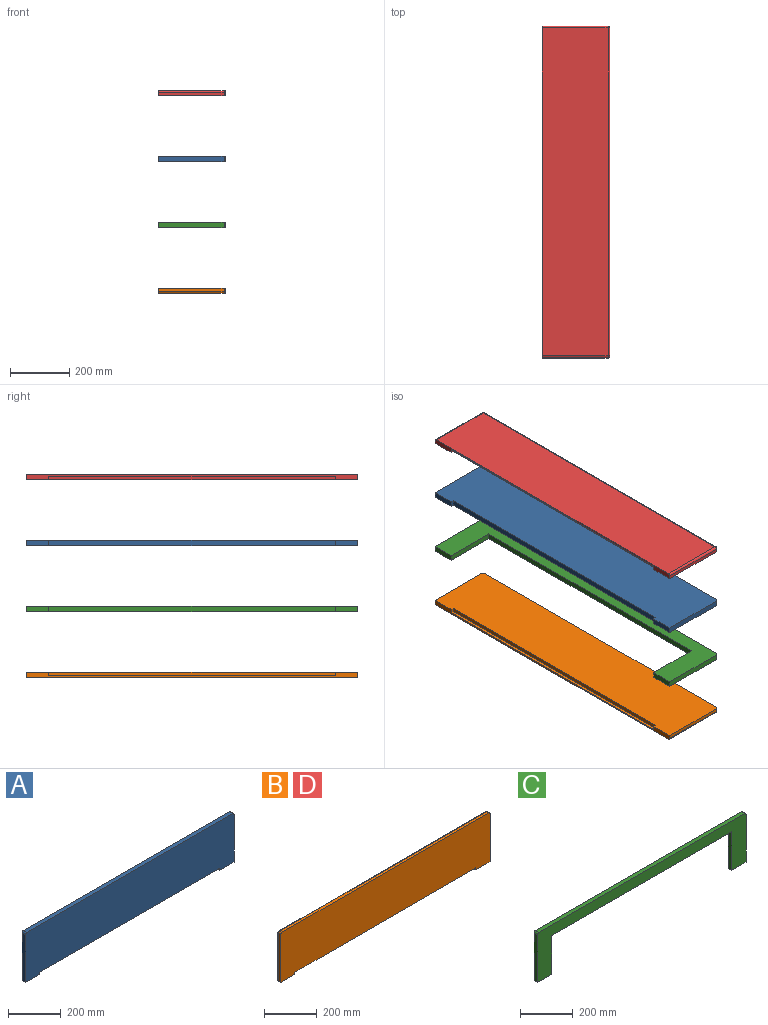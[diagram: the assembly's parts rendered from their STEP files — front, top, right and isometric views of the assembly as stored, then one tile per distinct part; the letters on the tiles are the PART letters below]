
ASSEMBLY  parts=4 mates=3
PART A: 12 faces, bbox 1117.6x19.1x228.6 mm
  f0: plane 76.2x19.05mm, normal (0,0,-1), area 1451.6mm2, adj f2,f3,f5,f7
  f1: plane 76.2x19.05mm, normal (0,0,-1), area 1451.6mm2, adj f2,f3,f6,f8
  f2: plane 1117.6x228.6mm, normal (0,-1,0), area 246272.5mm2, adj f0,f1,f4,f5,f6,f7,f8,f9
  f3: plane 1117.6x228.6mm, normal (0,1,0), area 246272.5mm2, adj f0,f1,f4,f5,f6,f7,f8,f9
  f4: plane 1104.9x19.05mm, normal (0,0,1), area 21048.3mm2, adj f2,f3,f10,f11
  f5: plane 222.25x19.05mm, normal (-1,0,0), area 4233.9mm2, adj f0,f2,f3,f11
  f6: plane 222.25x19.05mm, normal (1,0,0), area 4233.9mm2, adj f1,f2,f3,f10
  f7: plane 19.05x9.53mm, normal (1,0,0), area 181.5mm2, adj f0,f2,f3,f9
  f8: plane 19.05x9.53mm, normal (-1,0,0), area 181.5mm2, adj f1,f2,f3,f9
  f9: plane 965.2x19.05mm, normal (0,0,-1), area 18387.1mm2, adj f2,f3,f7,f8
  f10: cylinder r=6.35mm len=19.05mm, axis (0,-1,0), area 190mm2, adj f2,f3,f4,f6
  f11: cylinder r=6.35mm len=19.05mm, axis (0,1,0), area 190mm2, adj f2,f3,f4,f5
PART B: 17 faces, bbox 1117.6x17.8x228.6 mm
  f0: plane 1117.6x228.6mm, normal (0,-1,0), area 246272.5mm2, adj f1,f2,f3,f5,f6,f7,f8,f11
  f1: plane 1117.6x17.78mm, normal (0,0,-1), area 7595.6mm2, adj f0,f2,f3,f4,f6,f7,f9,f10
  f2: plane 222.25x11.43mm, normal (1,0,0), area 2540.3mm2, adj f0,f1,f10,f11
  f3: plane 222.25x11.43mm, normal (-1,0,0), area 2540.3mm2, adj f0,f1,f14,f16
  f4: plane 1104.9x222.25mm, normal (0,1,0), area 245564mm2, adj f1,f10,f13,f16
  f5: plane 1104.9x11.43mm, normal (0,0,1), area 12629mm2, adj f0,f11,f13,f14
  f6: plane 12.7x9.53mm, normal (1,0,0), area 121mm2, adj f0,f1,f8,f9
  f7: plane 12.7x9.53mm, normal (-1,0,0), area 121mm2, adj f0,f1,f8,f9
  f8: plane 965.2x12.7mm, normal (0,0,-1), area 12258mm2, adj f0,f6,f7,f9
  f9: plane 965.2x9.53mm, normal (0,-1,0), area 9193.5mm2, adj f1,f6,f7,f8
  f10: cylinder r=6.35mm len=222.25mm, axis (0,0,-1), area 2216.8mm2, adj f1,f2,f4,f12
  f11: cylinder r=6.35mm len=11.43mm, axis (0,1,0), area 114mm2, adj f0,f2,f5,f12
  f12: sphere r=6.35mm, area 63.3mm2, adj f10,f11,f13
  f13: cylinder r=6.35mm len=1104.9mm, axis (-1,0,0), area 11020.9mm2, adj f4,f5,f12,f15
  f14: cylinder r=6.35mm len=11.43mm, axis (0,-1,0), area 114mm2, adj f0,f3,f5,f15
  f15: sphere r=6.35mm, area 63.3mm2, adj f13,f14,f16
  f16: cylinder r=6.35mm len=222.25mm, axis (0,0,1), area 2216.8mm2, adj f1,f3,f4,f15
PART C: 12 faces, bbox 1117.6x19.1x228.6 mm
  f0: plane 965.2x19.05mm, normal (0,0,-1), area 18387.1mm2, adj f1,f7,f8,f9
  f1: plane 179.39x19.05mm, normal (-1,0,0), area 3417.3mm2, adj f0,f2,f8,f9
  f2: plane 76.2x19.05mm, normal (0,0,-1), area 1451.6mm2, adj f1,f3,f8,f9
  f3: plane 222.25x19.05mm, normal (1,0,0), area 4233.9mm2, adj f2,f8,f9,f10
  f4: plane 1104.9x19.05mm, normal (0,0,1), area 21048.3mm2, adj f8,f9,f10,f11
  f5: plane 222.25x19.05mm, normal (-1,0,0), area 4233.9mm2, adj f6,f8,f9,f11
  f6: plane 76.2x19.05mm, normal (0,0,-1), area 1451.6mm2, adj f5,f7,f8,f9
  f7: plane 179.39x19.05mm, normal (1,0,0), area 3417.3mm2, adj f0,f6,f8,f9
  f8: plane 1117.6x228.6mm, normal (0,-1,0), area 82321.2mm2, adj f0,f1,f2,f3,f4,f5,f6,f7
  f9: plane 1117.6x228.6mm, normal (0,1,0), area 82321.2mm2, adj f0,f1,f2,f3,f4,f5,f6,f7
  f10: cylinder r=6.35mm len=19.05mm, axis (0,1,0), area 190mm2, adj f3,f4,f8,f9
  f11: cylinder r=6.35mm len=19.05mm, axis (0,-1,0), area 190mm2, adj f4,f5,f8,f9
PART D: same geometry as B
PLACE A rot(axis=(0.58,0.58,0.58),120deg) t=(3.49,48.69,154.58)mm
PLACE B rot(axis=(-0.58,0.58,-0.58),120deg) t=(3.49,861.49,-261.66)mm
PLACE C rot(axis=(-0.58,0.58,-0.58),120deg) t=(3.49,861.49,-77.51)mm
PLACE D rot(axis=(0.58,0.58,0.58),120deg) t=(3.49,48.69,357.78)mm
MATE fastened C.f4 <-> B.f5  axis (1,0,0) through (228.92,455.09,-72.59)mm
MATE fastened D.f5 <-> A.f4  axis (1,0,0) through (228.92,455.09,371.91)mm
MATE fastened A.f4 <-> C.f4  axis (1,0,0) through (228.92,455.09,149.66)mm
